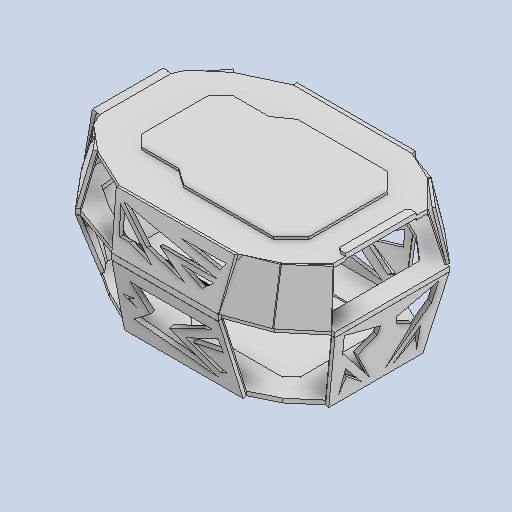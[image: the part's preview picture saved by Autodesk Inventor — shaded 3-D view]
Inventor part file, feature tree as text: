
AUTODESK INVENTOR PART (.ipt)
format: ipt  version: 2025.2 (Build 292293000, 293)  size: 949,248 bytes
history: native  units: mm
features: other x3, sketch x1
ambient origin geometry x8: Origin, YZ Plane, XZ Plane, XY Plane, X Axis, Y Axis, Z Axis, Center Point
bodies: Body1 (feature_tree)
feature tree (4):
  other  "Part1EDDv3.ipt"
  sketch  "Sketch1"  dims[d0=5.0mm d1=0.5mm]
  other  "Solid2::Part1EDDv3.ipt"
  other  "TaggingFeature1"
